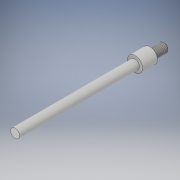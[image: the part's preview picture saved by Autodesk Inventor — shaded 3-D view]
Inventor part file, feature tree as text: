
AUTODESK INVENTOR PART (.ipt)
format: ipt  version: 2019 (Build 230136000, 136)  size: 108,032 bytes
history: native  units: mm
features: other x2, chamfer x1, sketch x1
ambient origin geometry x8: Origin, YZ Plane, XZ Plane, XY Plane, X Axis, Y Axis, Z Axis, Center Point
bodies: Solide1 (feature_tree)
feature tree (4):
  other  "Révolution1"
  other  "Filetage1"
  chamfer  "Chanfrein1"  Distance=3.0mm
  sketch  "Esquisse2"
